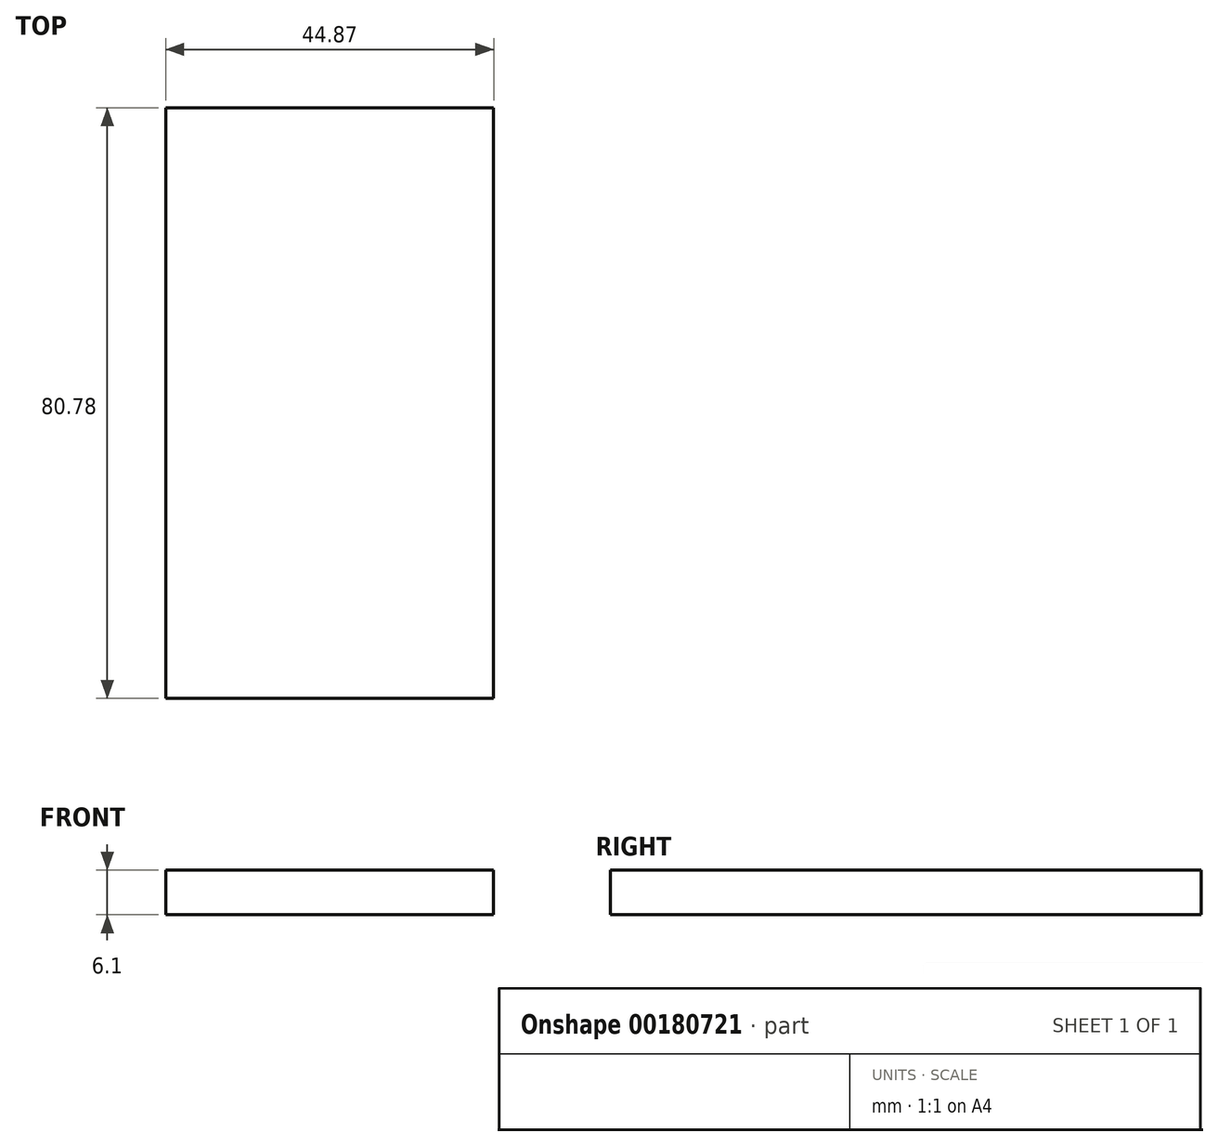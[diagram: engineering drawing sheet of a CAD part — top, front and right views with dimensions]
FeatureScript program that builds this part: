
annotation { "Feature Type Name" : "Feature", "Feature Type Description" : "" }
export const myFeature = defineFeature(function(context is Context, id is Id, definition is map)
    precondition{}
    {
        {
            var Q0;
            Q0=qCreatedBy(makeId("Top.planeOp"),FACE);
            var sketch = newSketch(context, id + "F0", { "sketchPlane" : qUnion([Q0])});
            skLineSegment(sketch, "E0.bottom", {"start": v(-65.53, 41.94) * mm, "end": v(-20.66, 41.94) * mm});
            skLineSegment(sketch, "E0.top", {"start": v(-65.53, -38.84) * mm, "end": v(-20.66, -38.84) * mm});
            skLineSegment(sketch, "E0.left", {"start": v(-65.53, 41.94) * mm, "end": v(-65.53, -38.84) * mm});
            skLineSegment(sketch, "E0.right", {"start": v(-20.66, 41.94) * mm, "end": v(-20.66, -38.84) * mm});
            skSolve(sketch);
        }
        {
            var Q0;
            Q0=makeQuery(id+"F0.imprint","IMPRINT",FACE,{"disambiguationData":[TD([[makeQuery(id+"F0.imprint","IMPRINT",EDGE,{"derivedFrom":sQuery(id+"F0.wireOp",EDGE,"E0.bottom")}),-1.0]])]});
            extrude(context, id + "F1", {"entities" : qUnion([Q0]), "depth" : 6.1 * mm});
        }
    });
